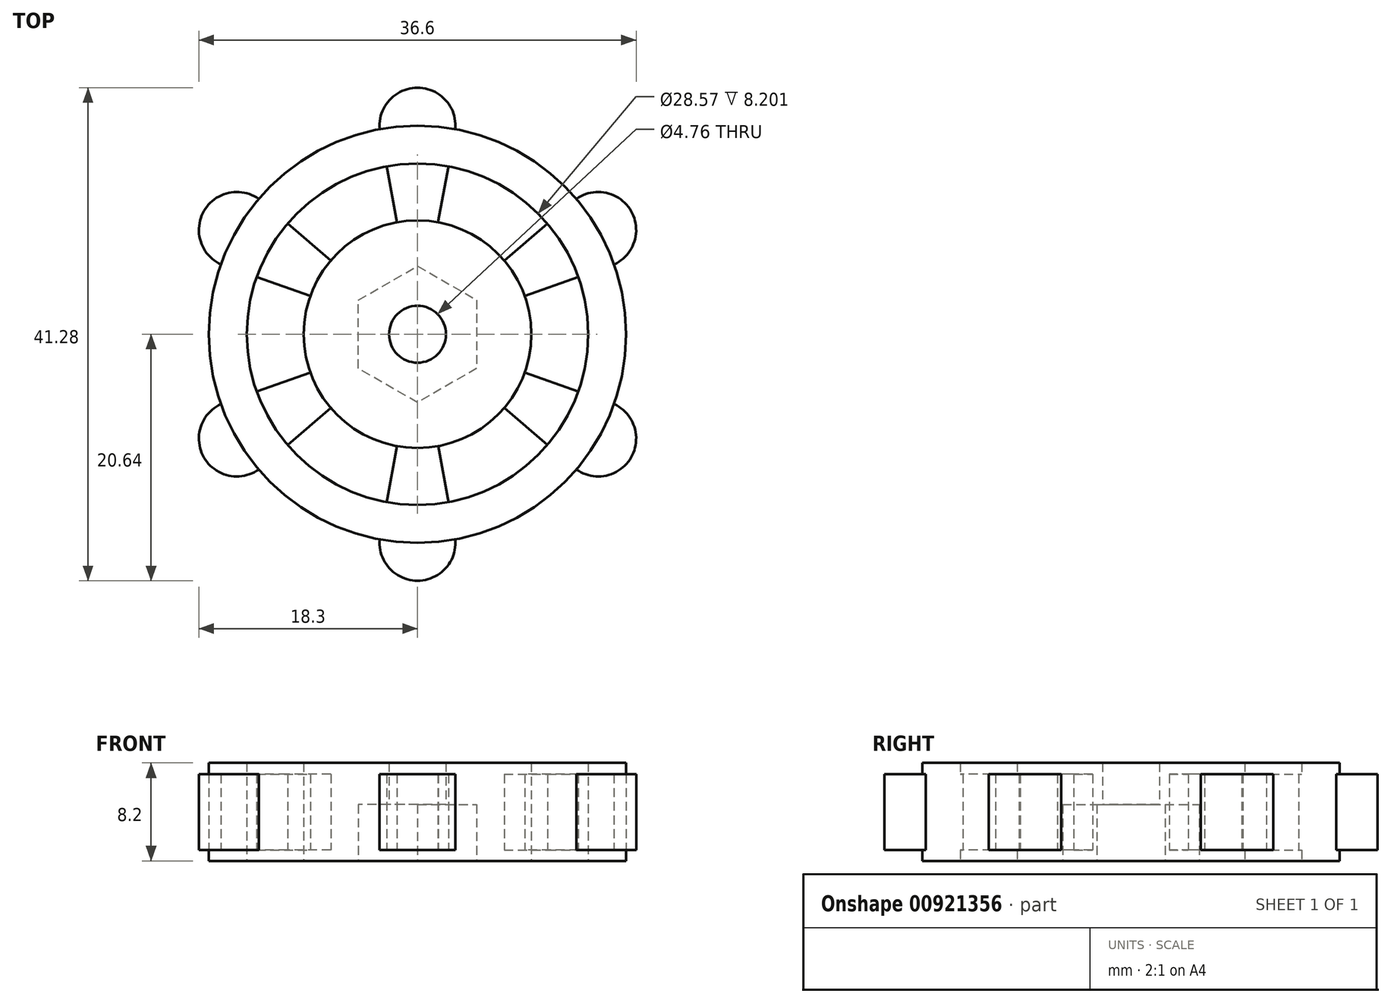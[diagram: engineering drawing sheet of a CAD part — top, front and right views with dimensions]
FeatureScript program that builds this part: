
annotation { "Feature Type Name" : "Feature", "Feature Type Description" : "" }
export const myFeature = defineFeature(function(context is Context, id is Id, definition is map)
    precondition{}
    {
        {
            var Q0;
            Q0=qCreatedBy(makeId("Top.planeOp"),FACE);
            var sketch = newSketch(context, id + "F0", { "sketchPlane" : qUnion([Q0])});
            skLineSegment(sketch, "E0", {"start": v(-4.95, -2.86) * mm, "end": v(-4.95, 2.86) * mm});
            skLineSegment(sketch, "E1", {"start": v(-4.95, 2.86) * mm, "end": v(0, 5.72) * mm});
            skLineSegment(sketch, "E2", {"start": v(0, 5.71) * mm, "end": v(4.95, 2.86) * mm});
            skLineSegment(sketch, "E3", {"start": v(4.95, 2.86) * mm, "end": v(4.95, -2.86) * mm});
            skLineSegment(sketch, "E4", {"start": v(4.95, -2.86) * mm, "end": v(0, -5.72) * mm});
            skLineSegment(sketch, "E5", {"start": v(0, -5.72) * mm, "end": v(-4.95, -2.86) * mm});
            skPoint(sketch, "E6.center.orphan", {"position": v(0, 0) * mm});
            skCircle(sketch, "E7", {"center": v(0, 0) * mm, "radius": 14.29 * mm});
            skCircle(sketch, "E8", {"center": v(0, 0) * mm, "radius": 17.46 * mm});
            skCircle(sketch, "E9", {"center": v(0, 0) * mm, "radius": 9.53 * mm});
            skSolve(sketch);
        }
        {
            var Q0;
            Q0=makeQuery(id+"F0.imprint","IMPRINT",FACE,{"disambiguationData":[TD([[makeQuery(id+"F0.imprint","IMPRINT",EDGE,{"derivedFrom":sQuery(id+"F0.wireOp",EDGE,"E7")}),-1.0]])]});
            var Q1;
            Q1=makeQuery(id+"F0.imprint","IMPRINT",FACE,{"disambiguationData":[TD([[makeQuery(id+"F0.imprint","IMPRINT",EDGE,{"derivedFrom":sQuery(id+"F0.wireOp",EDGE,"NPPQVDgX-Aatv-nky2-VCyc-h6sgwvsCMMmk")}),-1.0]])]});
            var Q2;
            Q2=makeQuery(id+"F0.imprint","IMPRINT",FACE,{"disambiguationData":[TD([[makeQuery(id+"F0.imprint","IMPRINT",EDGE,{"derivedFrom":sQuery(id+"F0.wireOp",EDGE,"E0")}),1.0]])]});
            extrude(context, id + "F1", {"entities" : qUnion([Q0, Q1, Q2]), "depth" : (5.08 - .3715) * mm, "offsetDistance" : 25.4 * mm});
        }
        {
            var Q0;
            Q0=makeQuery(id+"F1.opExtrude","CAP_FACE",FACE,{"disambiguationData":[OSD([sQuery(id+"F0.wireOp",EDGE,"E9")])],"isStart":false});
            var sketch = newSketch(context, id + "F2", { "sketchPlane" : qUnion([Q0])});
            skArc(sketch, "E10", {"start": v(-3.16, -17.17) * mm, "mid": v(0, -20.64) * mm, "end": v(3.16, -17.17) * mm});
            skCircle(sketch, "E11", {"center": v(0, 0) * mm, "radius": 17.46 * mm});
            skLineSegment(sketch, "E12", {"start": v(-1.71, -9.37) * mm, "end": v(-2.58, -14.05) * mm});
            skArc(sketch, "E13.1.0", {"start": v(13.3, -11.33) * mm, "mid": v(17.87, -10.32) * mm, "end": v(16.45, -5.85) * mm});
            skLineSegment(sketch, "E13.1.1", {"start": v(7.26, -6.17) * mm, "end": v(10.88, -9.26) * mm});
            skArc(sketch, "E13.2.0", {"start": v(16.45, 5.85) * mm, "mid": v(17.87, 10.32) * mm, "end": v(13.3, 11.33) * mm});
            skLineSegment(sketch, "E13.2.1", {"start": v(8.97, 3.2) * mm, "end": v(13.46, 4.79) * mm});
            skArc(sketch, "E13.3.0", {"start": v(3.16, 17.17) * mm, "mid": v(0, 20.64) * mm, "end": v(-3.16, 17.17) * mm});
            skLineSegment(sketch, "E13.3.1", {"start": v(1.71, 9.37) * mm, "end": v(2.58, 14.05) * mm});
            skArc(sketch, "E13.4.0", {"start": v(-13.3, 11.33) * mm, "mid": v(-17.87, 10.32) * mm, "end": v(-16.45, 5.85) * mm});
            skLineSegment(sketch, "E13.4.1", {"start": v(-7.26, 6.17) * mm, "end": v(-10.88, 9.26) * mm});
            skArc(sketch, "E13.5.0", {"start": v(-16.45, -5.85) * mm, "mid": v(-17.87, -10.32) * mm, "end": v(-13.3, -11.33) * mm});
            skLineSegment(sketch, "E13.5.1", {"start": v(-8.97, -3.2) * mm, "end": v(-13.46, -4.79) * mm});
            skCircle(sketch, "E14", {"center": v(0, 0) * mm, "radius": 9.53 * mm});
            skLineSegment(sketch, "E15", {"start": v(1.72, -9.37) * mm, "end": v(2.59, -14.05) * mm});
            skCircle(sketch, "E16", {"center": v(0, 0) * mm, "radius": 14.29 * mm});
            skLineSegment(sketch, "E17.trimOffspring", {"start": v(13.46, -4.79) * mm, "end": v(8.97, -3.2) * mm});
            skLineSegment(sketch, "E18.trimOffspring", {"start": v(10.88, 9.26) * mm, "end": v(7.26, 6.17) * mm});
            skLineSegment(sketch, "E19.trimOffspring", {"start": v(-2.58, 14.05) * mm, "end": v(-1.71, 9.37) * mm});
            skLineSegment(sketch, "E20.trimOffspring", {"start": v(-13.46, 4.79) * mm, "end": v(-8.97, 3.2) * mm});
            skLineSegment(sketch, "E21.trimOffspring", {"start": v(-10.88, -9.26) * mm, "end": v(-7.26, -6.17) * mm});
            skCircle(sketch, "E22", {"center": v(0, 0) * mm, "radius": 2.38 * mm});
            skSolve(sketch);
        }
        {
            var Q0;
            {var subQ0=sQuery(id+"F2.wireOp",EDGE,"E10");Q0=makeQuery(id+"F2.imprint","IMPRINT",FACE,{"disambiguationData":[TD([[makeQuery(id+"F2.imprint","IMPRINT",EDGE,{"derivedFrom":subQ0}),1.0]])]});}
            var Q1;
            {var subQ0=sQuery(id+"F2.wireOp",EDGE,"E13.5.0");var subQ1=sQuery(id+"F2.wireOp",EDGE,"E11");var subQ2=makeQuery(id+"F2.imprint","INTERSECT",VERTEX,{"derivedFrom":[subQ1,subQ0,sQuery(id+"F2.wireOp",EDGE,"E13.5.2")]});Q1=makeQuery(id+"F2.imprint","IMPRINT",FACE,{"disambiguationData":[TD([[makeQuery(id+"F2.imprint","IMPRINT",EDGE,{"disambiguationData":[TD([[subQ2,1.0]])],"derivedFrom":subQ1}),-1.0]])]});}
            var Q2;
            {var subQ0=sQuery(id+"F2.wireOp",EDGE,"E13.4.0");var subQ1=sQuery(id+"F2.wireOp",EDGE,"E11");var subQ2=makeQuery(id+"F2.imprint","INTERSECT",VERTEX,{"derivedFrom":[subQ1,subQ0,sQuery(id+"F2.wireOp",EDGE,"E13.4.2")]});Q2=makeQuery(id+"F2.imprint","IMPRINT",FACE,{"disambiguationData":[TD([[makeQuery(id+"F2.imprint","IMPRINT",EDGE,{"disambiguationData":[TD([[subQ2,1.0]])],"derivedFrom":subQ1}),-1.0]])]});}
            var Q3;
            {var subQ0=sQuery(id+"F2.wireOp",EDGE,"E13.3.0");var subQ1=sQuery(id+"F2.wireOp",EDGE,"E11");var subQ2=makeQuery(id+"F2.imprint","INTERSECT",VERTEX,{"derivedFrom":[subQ1,subQ0,sQuery(id+"F2.wireOp",EDGE,"E13.3.2")]});Q3=makeQuery(id+"F2.imprint","IMPRINT",FACE,{"disambiguationData":[TD([[makeQuery(id+"F2.imprint","IMPRINT",EDGE,{"disambiguationData":[TD([[subQ2,1.0]])],"derivedFrom":subQ1}),-1.0]])]});}
            var Q4;
            {var subQ0=sQuery(id+"F2.wireOp",EDGE,"E13.2.0");var subQ1=sQuery(id+"F2.wireOp",EDGE,"E11");var subQ2=makeQuery(id+"F2.imprint","INTERSECT",VERTEX,{"derivedFrom":[subQ1,subQ0,sQuery(id+"F2.wireOp",EDGE,"E13.2.2")]});Q4=makeQuery(id+"F2.imprint","IMPRINT",FACE,{"disambiguationData":[TD([[makeQuery(id+"F2.imprint","IMPRINT",EDGE,{"disambiguationData":[TD([[subQ2,1.0]])],"derivedFrom":subQ1}),-1.0]])]});}
            var Q5;
            {var subQ0=sQuery(id+"F2.wireOp",EDGE,"E13.1.0");Q5=makeQuery(id+"F2.imprint","IMPRINT",FACE,{"disambiguationData":[TD([[makeQuery(id+"F2.imprint","IMPRINT",EDGE,{"derivedFrom":subQ0}),1.0]])]});}
            var Q6;
            {var subQ0=sQuery(id+"F2.wireOp",EDGE,"E13.1.1");Q6=makeQuery(id+"F2.imprint","IMPRINT",FACE,{"disambiguationData":[TD([[makeQuery(id+"F2.imprint","IMPRINT",EDGE,{"derivedFrom":subQ0}),1.0]])]});}
            var Q7;
            {var subQ0=sQuery(id+"F2.wireOp",EDGE,"E13.2.1");Q7=makeQuery(id+"F2.imprint","IMPRINT",FACE,{"disambiguationData":[TD([[makeQuery(id+"F2.imprint","IMPRINT",EDGE,{"derivedFrom":subQ0}),1.0]])]});}
            var Q8;
            {var subQ0=sQuery(id+"F2.wireOp",EDGE,"E13.3.1");Q8=makeQuery(id+"F2.imprint","IMPRINT",FACE,{"disambiguationData":[TD([[makeQuery(id+"F2.imprint","IMPRINT",EDGE,{"derivedFrom":subQ0}),1.0]])]});}
            var Q9;
            {var subQ0=sQuery(id+"F2.wireOp",EDGE,"E13.5.1");Q9=makeQuery(id+"F2.imprint","IMPRINT",FACE,{"disambiguationData":[TD([[makeQuery(id+"F2.imprint","IMPRINT",EDGE,{"derivedFrom":subQ0}),1.0]])]});}
            var Q10;
            {var subQ0=sQuery(id+"F2.wireOp",EDGE,"E12");Q10=makeQuery(id+"F2.imprint","IMPRINT",FACE,{"disambiguationData":[TD([[makeQuery(id+"F2.imprint","IMPRINT",EDGE,{"derivedFrom":subQ0}),1.0]])]});}
            var Q11;
            {var subQ0=sQuery(id+"F2.wireOp",EDGE,"E11");var subQ1=sQuery(id+"F2.wireOp",EDGE,"E13.5.0");var subQ2=makeQuery(id+"F2.imprint","INTERSECT",VERTEX,{"derivedFrom":[subQ1,sQuery(id+"F2.wireOp",EDGE,"E13.5.2"),subQ0]});Q11=makeQuery(id+"F2.imprint","IMPRINT",FACE,{"disambiguationData":[TD([[makeQuery(id+"F2.imprint","IMPRINT",EDGE,{"disambiguationData":[TD([[subQ2,1.0]])],"derivedFrom":subQ1}),1.0]])]});}
            var Q12;
            {var subQ0=sQuery(id+"F2.wireOp",EDGE,"E11");var subQ1=sQuery(id+"F2.wireOp",EDGE,"E13.4.0");var subQ2=makeQuery(id+"F2.imprint","INTERSECT",VERTEX,{"derivedFrom":[subQ1,sQuery(id+"F2.wireOp",EDGE,"E13.4.2"),subQ0]});Q12=makeQuery(id+"F2.imprint","IMPRINT",FACE,{"disambiguationData":[TD([[makeQuery(id+"F2.imprint","IMPRINT",EDGE,{"disambiguationData":[TD([[subQ2,1.0]])],"derivedFrom":subQ1}),1.0]])]});}
            var Q13;
            {var subQ0=sQuery(id+"F2.wireOp",EDGE,"E13.4.1");Q13=makeQuery(id+"F2.imprint","IMPRINT",FACE,{"disambiguationData":[TD([[makeQuery(id+"F2.imprint","IMPRINT",EDGE,{"derivedFrom":subQ0}),1.0]])]});}
            var Q14;
            {var subQ0=sQuery(id+"F2.wireOp",EDGE,"E11");var subQ1=sQuery(id+"F2.wireOp",EDGE,"E13.3.0");var subQ2=makeQuery(id+"F2.imprint","INTERSECT",VERTEX,{"derivedFrom":[subQ1,sQuery(id+"F2.wireOp",EDGE,"E13.3.2"),subQ0]});Q14=makeQuery(id+"F2.imprint","IMPRINT",FACE,{"disambiguationData":[TD([[makeQuery(id+"F2.imprint","IMPRINT",EDGE,{"disambiguationData":[TD([[subQ2,1.0]])],"derivedFrom":subQ1}),1.0]])]});}
            var Q15;
            {var subQ0=sQuery(id+"F2.wireOp",EDGE,"E11");var subQ1=sQuery(id+"F2.wireOp",EDGE,"E13.2.0");var subQ2=makeQuery(id+"F2.imprint","INTERSECT",VERTEX,{"derivedFrom":[subQ1,sQuery(id+"F2.wireOp",EDGE,"E13.2.2"),subQ0]});Q15=makeQuery(id+"F2.imprint","IMPRINT",FACE,{"disambiguationData":[TD([[makeQuery(id+"F2.imprint","IMPRINT",EDGE,{"disambiguationData":[TD([[subQ2,1.0]])],"derivedFrom":subQ1}),1.0]])]});}
            extrude(context, id + "F3", {"entities" : qUnion([Q0, Q1, Q2, Q3, Q4, Q5, Q6, Q7, Q8, Q9, Q10, Q11, Q12, Q13, Q14, Q15]), "depth" : 2.54 * mm, "offsetDistance" : 25.4 * mm, "hasSecondDirection" : true, "secondDirectionOppositeDirection" : true, "secondDirectionDepth" : 3.8 * mm});
        }
        {
            var Q0;
            Q0=makeQuery(id+"F2.imprint","IMPRINT",FACE,{"disambiguationData":[TD([[makeQuery(id+"F2.imprint","IMPRINT",EDGE,{"derivedFrom":makeQuery(id+"F1.opExtrude","CAP_EDGE",EDGE,{"disambiguationData":[OSD([sQuery(id+"F0.wireOp",EDGE,"E0")])],"isStart":false})}),1.0]])]});
            var Q1;
            {var subQ22=sQuery(id+"F2.wireOp",EDGE,"E13.2.2");Q1=makeQuery(id+"F2.imprint","IMPRINT",FACE,{"disambiguationData":[TD([[makeQuery(id+"F2.imprint","IMPRINT",EDGE,{"derivedFrom":subQ22}),1.0]])]});}
            var Q2;
            Q2=makeQuery(id+"F2.imprint","IMPRINT",FACE,{"disambiguationData":[TD([[makeQuery(id+"F2.imprint","IMPRINT",EDGE,{"derivedFrom":sQuery(id+"F2.wireOp",EDGE,"E22")}),-1.0]])]});
            var Q3;
            {var subQ10=sQuery(id+"F2.wireOp",EDGE,"E16");var subQ11=makeQuery(id+"F2.imprint","INTERSECT",VERTEX,{"derivedFrom":[sQuery(id+"F2.wireOp",EDGE,"E13.2.1"),subQ10]});Q3=makeQuery(id+"F2.imprint","IMPRINT",FACE,{"disambiguationData":[TD([[makeQuery(id+"F2.imprint","IMPRINT",EDGE,{"disambiguationData":[TD([[subQ11,-1.0]])],"derivedFrom":subQ10}),-1.0]])]});}
            extrude(context, id + "F4", {"entities" : qUnion([Q0, Q1, Q2, Q3]), "operationType" : NewBodyOperationType.ADD, "depth" : (3.17 + .3175) * mm, "offsetDistance" : 25.4 * mm});
        }
    });
